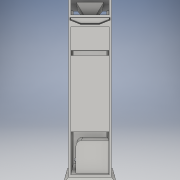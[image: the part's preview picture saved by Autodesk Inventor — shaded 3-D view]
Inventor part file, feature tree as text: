
AUTODESK INVENTOR PART (.ipt)
format: ipt  version: 2016 (Build 200138000, 138)  size: 482,816 bytes
history: native  units: in
note: dims shown in document units (in); Inventor stores cm internally (conversion verified against a paired STEP export)
features: sketch x20, extrude x18, chamfer x1, plane x1, loft x1, shell x1, fillet x1
ambient origin geometry x8: Origin, YZ Plane, XZ Plane, XY Plane, X Axis, Y Axis, Z Axis, Center Point
bodies: Solid1 (feature_tree)
feature tree (43):
  extrude  "Extrusion1"  Depth=18.0in
  extrude  "Extrusion3"  Depth=1.0in
  extrude  "Extrusion4"  Depth=1.0in
  extrude  "Extrusion7"  Depth=2.0in
  extrude  "Extrusion8"  Depth=16.2in
  chamfer  "Chamfer2"  Distance=13.3in
  extrude  "Extrusion9"  Depth=2.0in
  extrude  "Extrusion10"  Depth=2.0in TaperAngle=0.0deg
  sketch  "Sketch12"  dims[d13=2.0in]
  plane  "Work Plane1"
  loft  "Loft1"
  shell  "Shell1"  Thickness=17.0in
  extrude  "Extrusion12"  Depth=2.5in
  extrude  "Extrusion13"  Depth=2.5in
  extrude  "Extrusion14"  TaperAngle=0.0deg  [1 undecoded]
  extrude  "Extrusion15"  TaperAngle=0.0deg  [1 undecoded]
  extrude  "Extrusion16"  Depth=2.5in
  extrude  "Extrusion17"  Depth=2.5in TaperAngle=0.0deg
  extrude  "Extrusion18"  Depth=2.5in
  extrude  "Extrusion19"  Depth=2.5in TaperAngle=0.0deg
  extrude  "Extrusion20"  Depth=2.5in
  extrude  "Extrusion21"  Depth=2.5in
  extrude  "Extrusion22"  Depth=2.5in TaperAngle=0.0deg
  fillet  "Fillet1"  Radius=10.0in
  sketch  "Sketch1"  dims[d0=64.0in d1=18.0in]
  sketch  "Sketch3"  dims[d2=4.0in d3=1.0in]
  sketch  "Sketch4"  dims[d4=1.0in d5=1.0in]
  sketch  "Sketch7"  dims[d6=1.0in d7=2.0in]
  sketch  "Sketch8"  dims[d9=2.0in d10=16.2in]
  sketch  "Sketch9"  dims[d11=8.1in]
  sketch  "Sketch10"  dims[d12=2.56in]
  sketch  "Sketch13"  dims[d14=5.0in]
  sketch  "Sketch14"  dims[d15=5.0in]
  sketch  "Sketch15"  dims[d16=2.0in]
  sketch  "Sketch16"  dims[d17=18.0in]
  sketch  "Sketch17"  dims[d18=0.5in]
  sketch  "Sketch18"  dims[d19=0.5in d20=13.3in d21=0.0in]
  sketch  "Sketch19"  dims[d44=64.0in d45=18.0in d46=4.0in d47=1.0in d48=1.0in d49=1.0in d50=1.0in d51=2.0in d52=2.0in d54=16.2in d55=8.1in d56=2.56in d57=2.0in d58=5.0in d59=5.0in d60=2.0in d61=18.0in d62=0.5in d63=0.5in d64=0.85in d65=0.0in]
  sketch  "Sketch20"  dims[d66=64.0in d67=18.0in d68=4.0in d69=1.0in d70=1.0in d71=1.0in d72=1.0in d73=2.0in d74=2.0in d76=16.2in d77=8.1in d78=2.56in d79=2.0in d80=5.0in d81=5.0in d82=2.0in d83=18.0in d84=0.5in d85=0.5in d86=0.85in d87=0.0in d95=2.0in]
  sketch  "Sketch21"  dims[d96=2.0in d97=0.0in d98=2.0in d99=0.0in]
  sketch  "Sketch22"  dims[d100=2.0in d101=0.125in d102=45.0deg d103=0.5in d105=17.0in d106=0.0in]
  sketch  "Sketch23"  dims[d107=6.5in d108=0.0in d111=2.5in]
  sketch  "Sketch24"  dims[d112=6.5in d113=11.75in d114=0.0in d115=90.0deg d116=0.0in d117=90.0deg d118=0.005in d119=0.5in d120=0.0in d121=0.5in d122=16.0in d123=0.0in d124=0.5in d126=18.0in d127=16.0in d128=0.0in d129=10.0in d130=2.5in d131=8.3125in d132=0.0in d133=0.5in d134=4.0in d135=0.5in d136=1.5748in d138=360.0deg d140=2.0in d141=0.0in d144=1.5in d145=1.375in d146=0.0in d147=5.0in d148=2.0in d149=0.5in d150=13.5in d151=0.0in d153=0.5in d154=0.0in d155=3.0in d156=2.0in d157=2.0in d158=21.8125in d159=0.0in d163=14.0in d164=6.75in d165=2.0in d166=14.0in d167=0.0in d171=6.0in d172=0.005in d173=0.0in d174=2.5in d175=16.0in d176=0.5in]
note: 2 required parameter values undecoded (feature->parameter linkage not recoverable at this tier; creation-order binding heuristic only, values carry confidence <= 0.55)
